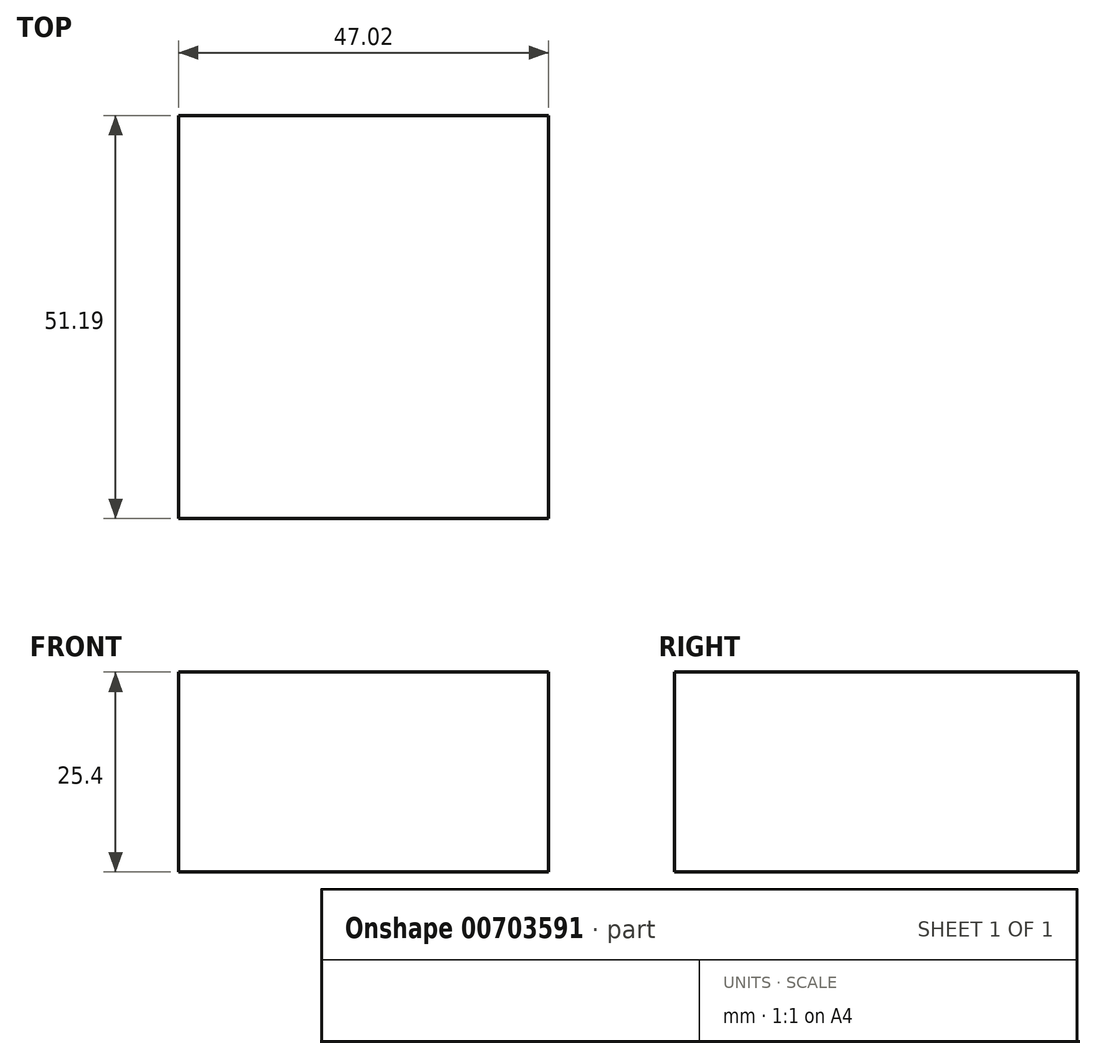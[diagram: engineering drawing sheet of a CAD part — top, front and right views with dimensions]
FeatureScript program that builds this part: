
annotation { "Feature Type Name" : "Feature", "Feature Type Description" : "" }
export const myFeature = defineFeature(function(context is Context, id is Id, definition is map)
    precondition{}
    {
        {
            var Q0;
            Q0=qCreatedBy(makeId("Top.planeOp"),FACE);
            var sketch = newSketch(context, id + "F0", { "sketchPlane" : qUnion([Q0])});
            skLineSegment(sketch, "E0.bottom", {"start": v(-9.95, 20) * mm, "end": v(-56.97, 20) * mm});
            skLineSegment(sketch, "E0.top", {"start": v(-9.95, 71.2) * mm, "end": v(-56.97, 71.2) * mm});
            skLineSegment(sketch, "E0.left", {"start": v(-9.95, 20) * mm, "end": v(-9.95, 71.2) * mm});
            skLineSegment(sketch, "E0.right", {"start": v(-56.97, 20) * mm, "end": v(-56.97, 71.2) * mm});
            skPoint(sketch, "E0.middle", {"position": v(-33.46, 45.6) * mm});
            skSolve(sketch);
        }
        {
            var Q0;
            Q0=makeQuery(id+"F0.imprint","IMPRINT",FACE,{"disambiguationData":[TD([[makeQuery(id+"F0.imprint","IMPRINT",EDGE,{"derivedFrom":sQuery(id+"F0.wireOp",EDGE,"E0.bottom")}),-1.0]])]});
            extrude(context, id + "F1", {"entities" : qUnion([Q0]), "depth" : 25.4 * mm, "offsetDistance" : 25.4 * mm});
        }
    });
